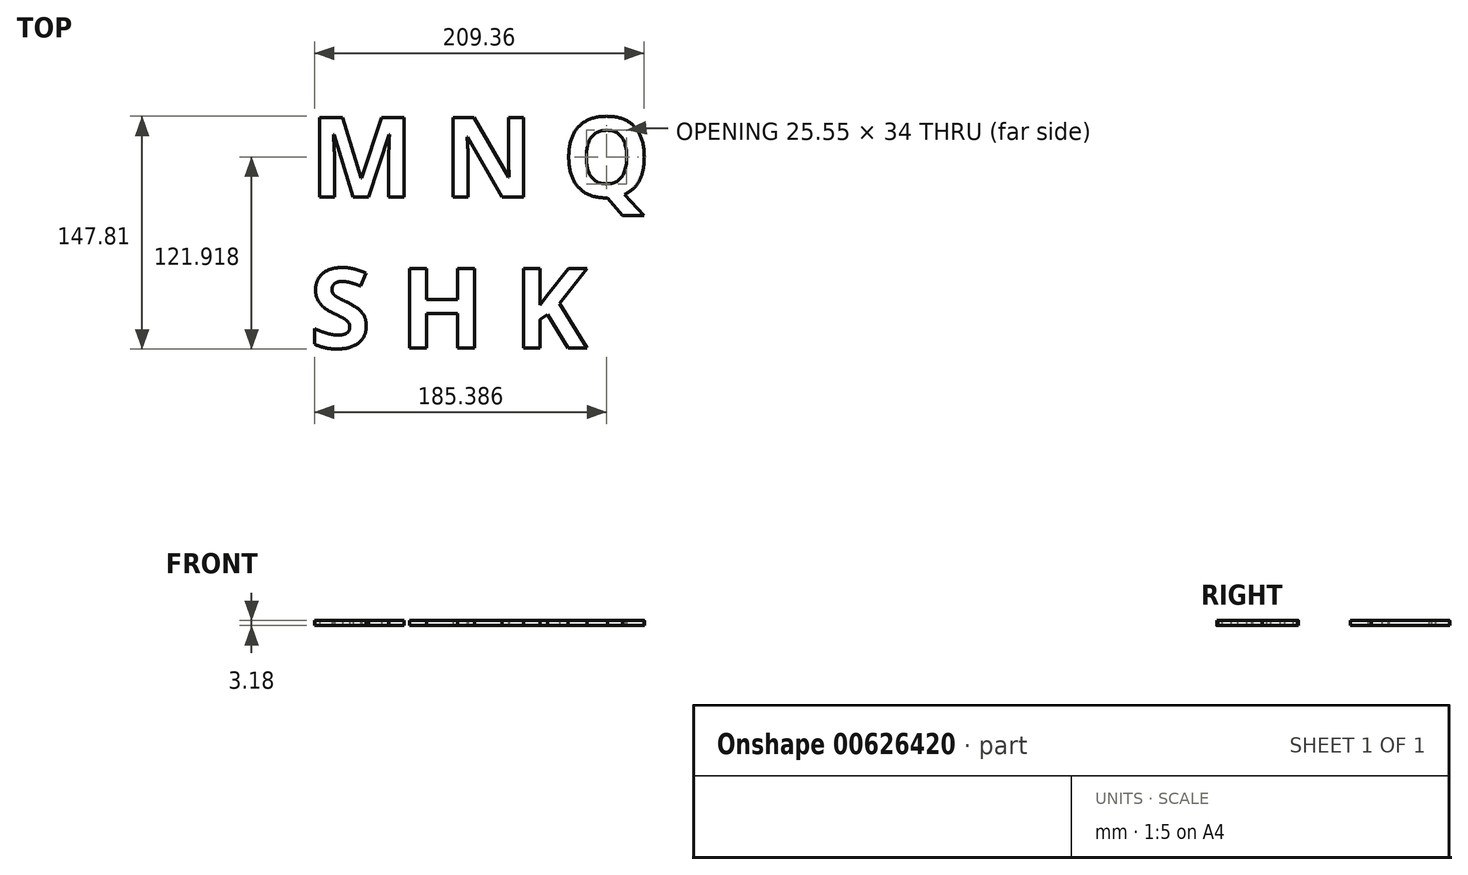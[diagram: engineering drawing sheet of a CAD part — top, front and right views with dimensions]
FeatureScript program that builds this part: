
annotation { "Feature Type Name" : "Feature", "Feature Type Description" : "" }
export const myFeature = defineFeature(function(context is Context, id is Id, definition is map)
    precondition{}
    {
        {
            var Q0;
            Q0=qCreatedBy(makeId("Top.planeOp"),FACE);
            var sketch = newSketch(context, id + "F0", { "sketchPlane" : qUnion([Q0])});
            skText(sketch, "E0", { "text": "M N Q\nS H K", "fontName": "OpenSans-Bold.ttf"});
            const initialGuessF0  = {"E0": [0, -0.0508, 1, 0, 0.0508]};
            skSetInitialGuess(sketch, initialGuessF0);
            skSolve(sketch);
        }
        {
            var Q0;
            Q0 = qSketchRegion(id + "F0", true);
            extrude(context, id + "F1", {"entities" : qUnion([Q0]), "depth" : 3.17 * mm, "offsetDistance" : 25.4 * mm});
        }
    });
